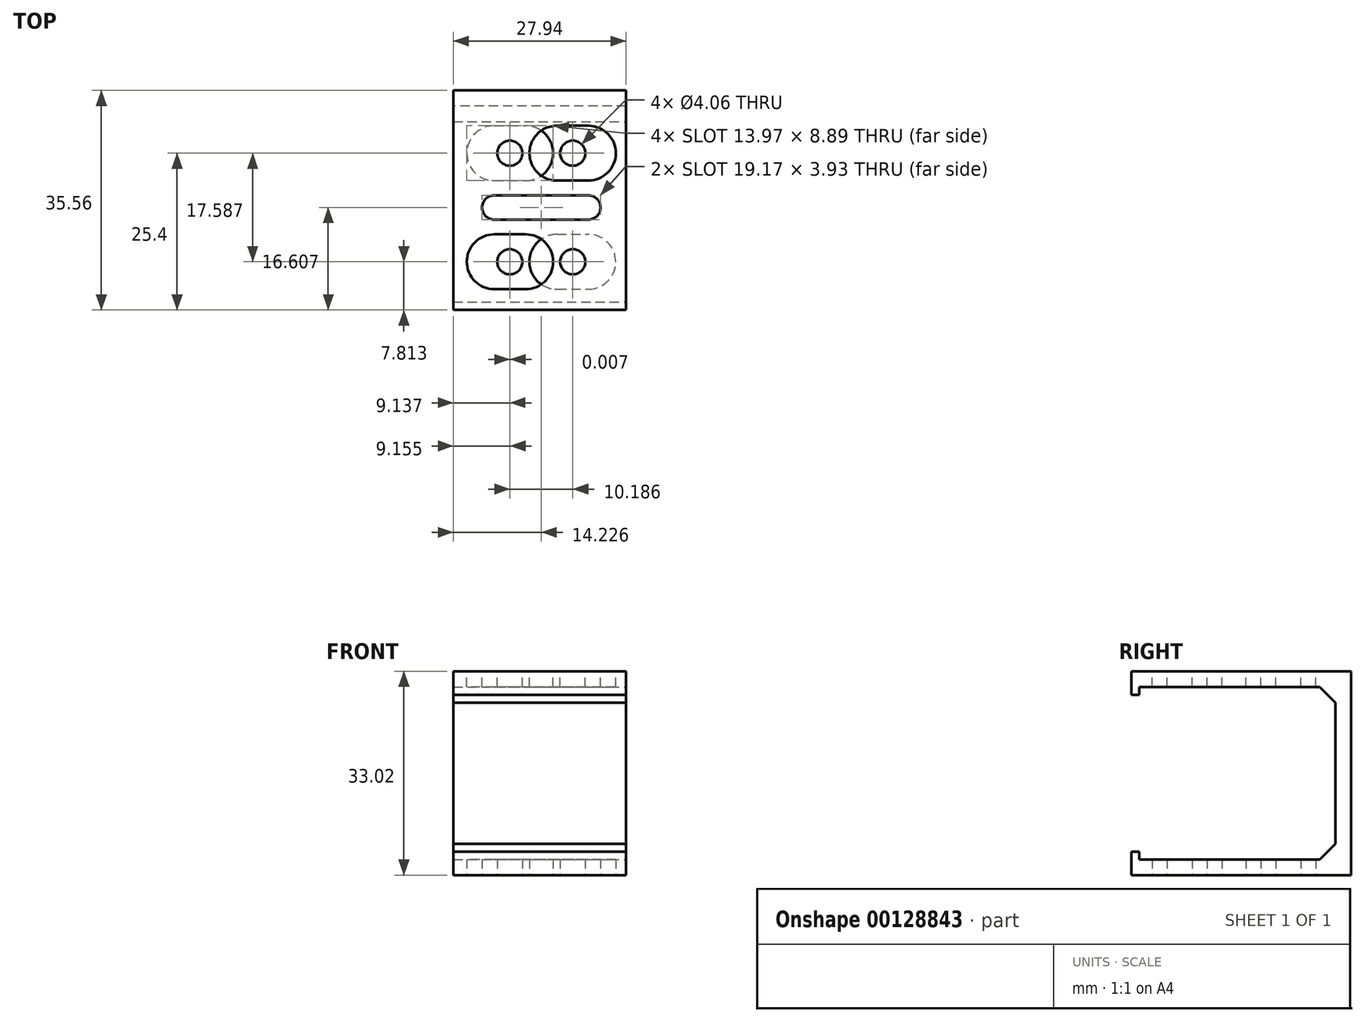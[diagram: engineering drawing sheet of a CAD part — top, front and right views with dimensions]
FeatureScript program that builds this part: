
annotation { "Feature Type Name" : "Feature", "Feature Type Description" : "" }
export const myFeature = defineFeature(function(context is Context, id is Id, definition is map)
    precondition{}
    {
        {
            var Q0;
            Q0=qCreatedBy(makeId("Right.planeOp"),FACE);
            var sketch = newSketch(context, id + "F0", { "sketchPlane" : qUnion([Q0])});
            skLineSegment(sketch, "E0", {"start": v(-35.56, 30.23) * mm, "end": v(0, 30.23) * mm});
            skLineSegment(sketch, "E1", {"start": v(0, 30.23) * mm, "end": v(0, -2.8) * mm});
            skLineSegment(sketch, "E2", {"start": v(0, -2.8) * mm, "end": v(-35.56, -2.8) * mm});
            skLineSegment(sketch, "E3.0", {"start": v(-2.54, -0.25) * mm, "end": v(-35.56, -0.25) * mm});
            skLineSegment(sketch, "E3.1", {"start": v(-2.54, 27.69) * mm, "end": v(-2.54, -0.25) * mm});
            skLineSegment(sketch, "E3.2", {"start": v(-35.56, 27.69) * mm, "end": v(-2.54, 27.69) * mm});
            skLineSegment(sketch, "E4", {"start": v(-35.56, 27.69) * mm, "end": v(-35.56, 30.23) * mm});
            skLineSegment(sketch, "E5", {"start": v(-35.56, -2.8) * mm, "end": v(-35.56, -0.25) * mm});
            skSolve(sketch);
        }
        {
            var Q0;
            Q0 = qSketchRegion(id + "F0", true);
            extrude(context, id + "F1", {"entities" : qUnion([Q0]), "depth" : 27.94 * mm});
        }
        {
            var Q0;
            Q0=makeQuery(id+"F1.opExtrude","SWEPT_FACE",FACE,{"disambiguationData":[OSD([sQuery(id+"F0.wireOp",EDGE,"E0")])]});
            var sketch = newSketch(context, id + "F2", { "sketchPlane" : qUnion([Q0])});
            skLineSegment(sketch, "E6.0", {"start": v(27.94, -2.54) * mm, "end": v(0, -2.54) * mm});
            skCircle(sketch, "E7", {"center": v(9.14, -10.16) * mm, "radius": 2.03 * mm});
            skCircle(sketch, "E8", {"center": v(19.32, -27.75) * mm, "radius": 2.03 * mm});
            skLineSegment(sketch, "E9.bottom", {"start": v(9.14, -10.16) * mm, "end": v(19.32, -10.16) * mm, "construction": true});
            skLineSegment(sketch, "E9.top", {"start": v(9.14, -27.75) * mm, "end": v(19.32, -27.75) * mm, "construction": true});
            skLineSegment(sketch, "E9.left", {"start": v(9.14, -10.16) * mm, "end": v(9.14, -27.75) * mm, "construction": true});
            skLineSegment(sketch, "E9.right", {"start": v(19.32, -10.16) * mm, "end": v(19.32, -27.75) * mm, "construction": true});
            skLineSegment(sketch, "E10.bottom", {"start": v(6.61, -16.99) * mm, "end": v(21.85, -16.99) * mm});
            skLineSegment(sketch, "E10.top", {"start": v(6.61, -20.92) * mm, "end": v(21.85, -20.92) * mm});
            skPoint(sketch, "E10.middle", {"position": v(14.23, -18.95) * mm});
            skPoint(sketch, "E10.middle.positionSnap0", {"position": v(19.32, -18.95) * mm});
            skPoint(sketch, "E10.middle.positionSnap1", {"position": v(14.23, -10.16) * mm});
            skPoint(sketch, "E10.centerSnap0", {"position": v(19.32, -18.95) * mm});
            skPoint(sketch, "E10.centerSnap1", {"position": v(14.23, -10.16) * mm});
            skArc(sketch, "E11", {"start": v(6.61, -16.99) * mm, "mid": v(4.65, -18.95) * mm, "end": v(6.61, -20.92) * mm});
            skArc(sketch, "E12", {"start": v(21.85, -20.92) * mm, "mid": v(23.82, -18.95) * mm, "end": v(21.85, -16.99) * mm});
            skLineSegment(sketch, "E13.bottom", {"start": v(21.88, -5.72) * mm, "end": v(16.8, -5.72) * mm});
            skLineSegment(sketch, "E13.top", {"start": v(21.84, -14.6) * mm, "end": v(16.76, -14.6) * mm});
            skPoint(sketch, "E13.middle", {"position": v(19.32, -10.16) * mm});
            skArc(sketch, "E14", {"start": v(16.8, -5.72) * mm, "mid": v(12.32, -10.14) * mm, "end": v(16.76, -14.6) * mm});
            skArc(sketch, "E15", {"start": v(21.84, -14.6) * mm, "mid": v(26.29, -10.18) * mm, "end": v(21.88, -5.72) * mm});
            skLineSegment(sketch, "E16.bottom", {"start": v(11.7, -23.3) * mm, "end": v(6.62, -23.3) * mm});
            skLineSegment(sketch, "E16.top", {"start": v(11.7, -32.2) * mm, "end": v(6.62, -32.2) * mm});
            skArc(sketch, "E17", {"start": v(6.62, -23.3) * mm, "mid": v(2.18, -27.75) * mm, "end": v(6.62, -32.2) * mm});
            skArc(sketch, "E18", {"start": v(11.7, -32.2) * mm, "mid": v(16.15, -27.75) * mm, "end": v(11.7, -23.3) * mm});
            skSolve(sketch);
        }
        {
            var Q0;
            Q0 = qSketchRegion(id + "F2", true);
            extrude(context, id + "F3", {"entities" : qUnion([Q0]), "operationType" : NewBodyOperationType.REMOVE, "endBound" : BoundingType.UP_TO_NEXT, "oppositeDirection" : true, "depth" : 25.4 * mm});
        }
        {
            var Q0;
            Q0=makeQuery(id+"F1.opExtrude","SWEPT_FACE",FACE,{"disambiguationData":[OSD([sQuery(id+"F0.wireOp",EDGE,"E2")])]});
            var sketch = newSketch(context, id + "F4", { "sketchPlane" : qUnion([Q0])});
            skLineSegment(sketch, "E19.0", {"start": v(27.94, 35.56) * mm, "end": v(0, 35.56) * mm});
            skCircle(sketch, "E20", {"center": v(9.14, 27.75) * mm, "radius": 2.03 * mm});
            skCircle(sketch, "E21", {"center": v(19.32, 10.16) * mm, "radius": 2.03 * mm});
            skLineSegment(sketch, "E22.bottom", {"start": v(9.14, 27.75) * mm, "end": v(19.32, 27.75) * mm, "construction": true});
            skLineSegment(sketch, "E22.top", {"start": v(9.14, 10.16) * mm, "end": v(19.32, 10.16) * mm, "construction": true});
            skLineSegment(sketch, "E22.left", {"start": v(9.14, 27.75) * mm, "end": v(9.14, 10.16) * mm, "construction": true});
            skLineSegment(sketch, "E22.right", {"start": v(19.32, 27.75) * mm, "end": v(19.32, 10.16) * mm, "construction": true});
            skLineSegment(sketch, "E23.bottom", {"start": v(6.6, 20.92) * mm, "end": v(21.85, 20.92) * mm});
            skLineSegment(sketch, "E23.top", {"start": v(6.6, 16.99) * mm, "end": v(21.85, 16.99) * mm});
            skPoint(sketch, "E23.middle", {"position": v(14.23, 18.95) * mm});
            skPoint(sketch, "E23.middle.positionSnap0", {"position": v(19.32, 18.95) * mm});
            skPoint(sketch, "E23.middle.positionSnap1", {"position": v(14.23, 27.75) * mm});
            skPoint(sketch, "E23.centerSnap0", {"position": v(19.32, 18.95) * mm});
            skPoint(sketch, "E23.centerSnap1", {"position": v(14.23, 27.75) * mm});
            skArc(sketch, "E24", {"start": v(6.6, 20.92) * mm, "mid": v(4.64, 18.95) * mm, "end": v(6.6, 16.99) * mm});
            skArc(sketch, "E25", {"start": v(21.85, 16.99) * mm, "mid": v(23.8, 18.95) * mm, "end": v(21.85, 20.92) * mm});
            skLineSegment(sketch, "E26.bottom", {"start": v(21.87, 32.2) * mm, "end": v(16.8, 32.2) * mm});
            skLineSegment(sketch, "E26.top", {"start": v(21.84, 23.3) * mm, "end": v(16.76, 23.3) * mm});
            skPoint(sketch, "E26.middle", {"position": v(19.32, 27.75) * mm});
            skArc(sketch, "E27", {"start": v(16.8, 32.2) * mm, "mid": v(12.31, 27.77) * mm, "end": v(16.76, 23.3) * mm});
            skArc(sketch, "E28", {"start": v(21.84, 23.3) * mm, "mid": v(26.28, 27.73) * mm, "end": v(21.87, 32.2) * mm});
            skLineSegment(sketch, "E29.bottom", {"start": v(11.7, 14.6) * mm, "end": v(6.62, 14.6) * mm});
            skLineSegment(sketch, "E29.top", {"start": v(11.7, 5.72) * mm, "end": v(6.62, 5.72) * mm});
            skArc(sketch, "E30", {"start": v(6.62, 14.6) * mm, "mid": v(2.17, 10.16) * mm, "end": v(6.62, 5.72) * mm});
            skArc(sketch, "E31", {"start": v(11.7, 5.72) * mm, "mid": v(16.14, 10.16) * mm, "end": v(11.7, 14.6) * mm});
            skLineSegment(sketch, "E32.25", {"start": v(27.94, 2.54) * mm, "end": v(0, 2.54) * mm});
            skSolve(sketch);
        }
        {
            var Q0;
            Q0 = qSketchRegion(id + "F4", true);
            extrude(context, id + "F5", {"entities" : qUnion([Q0]), "operationType" : NewBodyOperationType.REMOVE, "endBound" : BoundingType.UP_TO_NEXT, "oppositeDirection" : true, "depth" : 25.4 * mm});
        }
        {
            var Q0;
            Q0=makeQuery(id+"F1.opExtrude","SWEPT_EDGE",EDGE,{"disambiguationData":[OSD([sQuery(id+"F0.wireOp",EDGE,"E3.0"),sQuery(id+"F0.wireOp",EDGE,"E3.1")])]});
            var Q1;
            Q1=makeQuery(id+"F1.opExtrude","SWEPT_EDGE",EDGE,{"disambiguationData":[OSD([sQuery(id+"F0.wireOp",EDGE,"E3.1"),sQuery(id+"F0.wireOp",EDGE,"E3.2")])]});
            chamfer(context, id + "F6", {"entities" : qUnion([Q0, Q1]), "width" : 2.54 * mm, "tangentPropagation" : true});
        }
        {
            var Q0;
            Q0=makeQuery(id+"F1.opExtrude","SWEPT_FACE",FACE,{"disambiguationData":[OSD([sQuery(id+"F0.wireOp",EDGE,"E3.0")])]});
            var sketch = newSketch(context, id + "F7", { "sketchPlane" : qUnion([Q0])});
            skLineSegment(sketch, "E33", {"start": v(0, -34.29) * mm, "end": v(27.94, -34.29) * mm});
            skSolve(sketch);
        }
        {
            var Q0;
            {var subQ0=sQuery(id+"F7.wireOp",EDGE,"E33");Q0=makeQuery(id+"F7.imprint","IMPRINT",FACE,{"disambiguationData":[TD([[makeQuery(id+"F7.imprint","IMPRINT",EDGE,{"derivedFrom":subQ0}),-1.0]])]});}
            extrude(context, id + "F8", {"entities" : qUnion([Q0]), "operationType" : NewBodyOperationType.ADD, "depth" : 1.27 * mm});
        }
        {
            var Q0;
            Q0=makeQuery(id+"F1.opExtrude","SWEPT_FACE",FACE,{"disambiguationData":[OSD([sQuery(id+"F0.wireOp",EDGE,"E3.2")])]});
            var sketch = newSketch(context, id + "F9", { "sketchPlane" : qUnion([Q0])});
            skLineSegment(sketch, "E34", {"start": v(0, 34.3) * mm, "end": v(27.94, 34.3) * mm});
            skSolve(sketch);
        }
        {
            var Q0;
            {var subQ0=sQuery(id+"F9.wireOp",EDGE,"E34");Q0=makeQuery(id+"F9.imprint","IMPRINT",FACE,{"disambiguationData":[TD([[makeQuery(id+"F9.imprint","IMPRINT",EDGE,{"derivedFrom":subQ0}),1.0]])]});}
            extrude(context, id + "F10", {"entities" : qUnion([Q0]), "operationType" : NewBodyOperationType.ADD, "depth" : 1.27 * mm});
        }
    });
